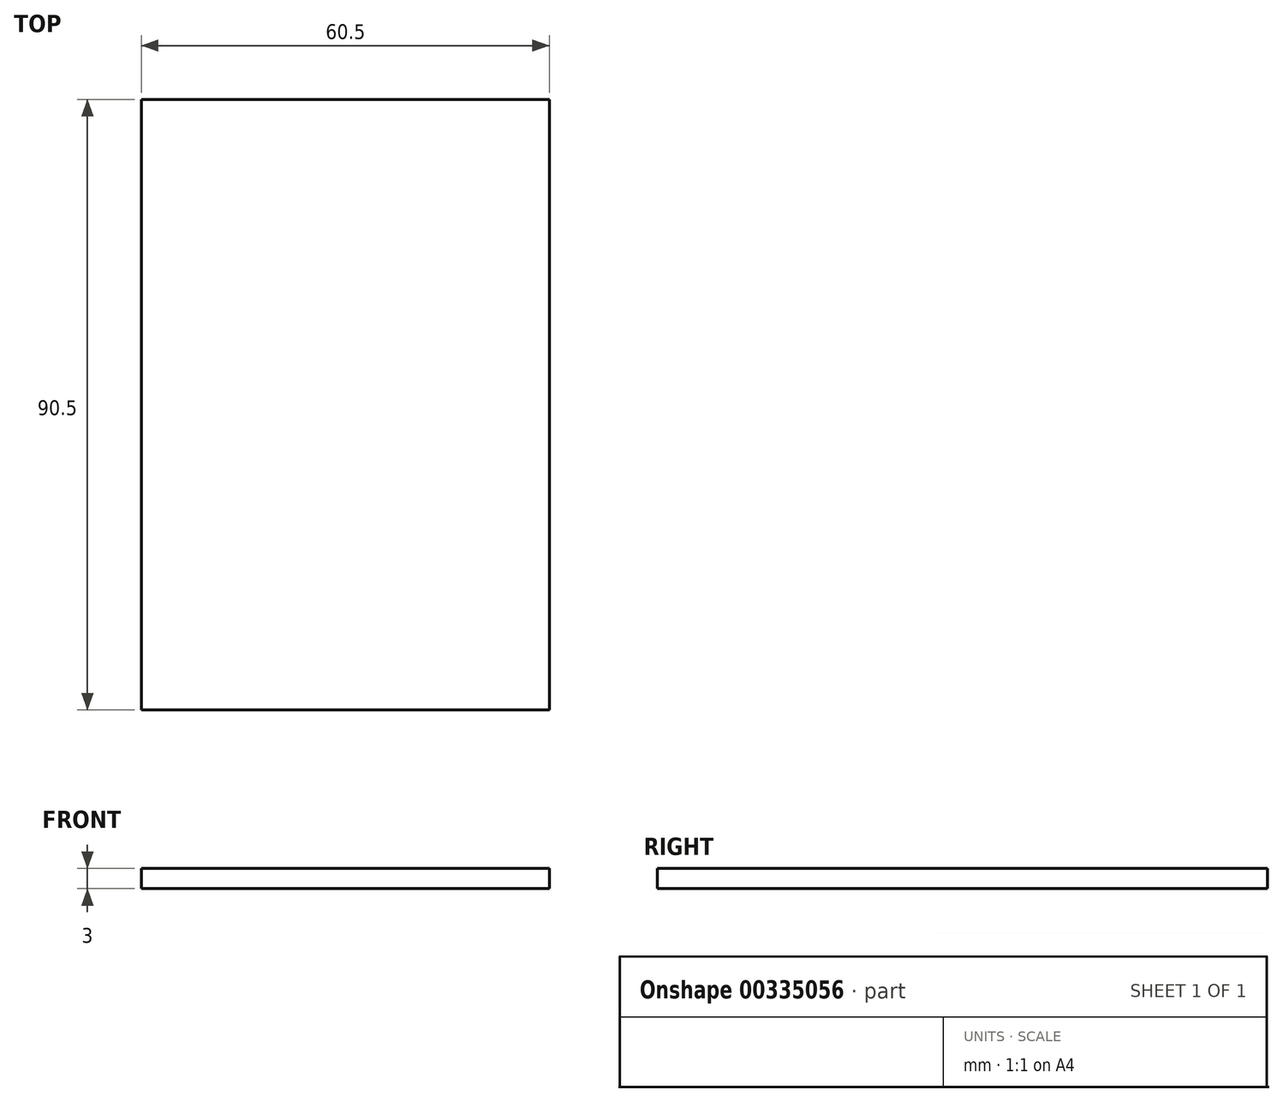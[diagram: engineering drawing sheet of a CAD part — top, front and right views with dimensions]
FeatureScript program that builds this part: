
annotation { "Feature Type Name" : "Feature", "Feature Type Description" : "" }
export const myFeature = defineFeature(function(context is Context, id is Id, definition is map)
    precondition{}
    {
        {
            var Q0;
            Q0=qCreatedBy(makeId("Top.planeOp"),FACE);
            var sketch = newSketch(context, id + "F0", { "sketchPlane" : qUnion([Q0])});
            skLineSegment(sketch, "E0.bottom", {"start": v(0, 0) * mm, "end": v(60.5, 0) * mm});
            skLineSegment(sketch, "E0.top", {"start": v(0, -90.5) * mm, "end": v(60.5, -90.5) * mm});
            skLineSegment(sketch, "E0.left", {"start": v(0, 0) * mm, "end": v(0, -90.5) * mm});
            skLineSegment(sketch, "E0.right", {"start": v(60.5, 0) * mm, "end": v(60.5, -90.5) * mm});
            skSolve(sketch);
        }
        {
            var Q0;
            Q0=makeQuery(id+"F0.imprint","IMPRINT",FACE,{"disambiguationData":[TD([[makeQuery(id+"F0.imprint","IMPRINT",EDGE,{"derivedFrom":sQuery(id+"F0.wireOp",EDGE,"E0.bottom")}),-1.0]])]});
            extrude(context, id + "F1", {"entities" : qUnion([Q0]), "depth" : 3 * mm});
        }
    });
